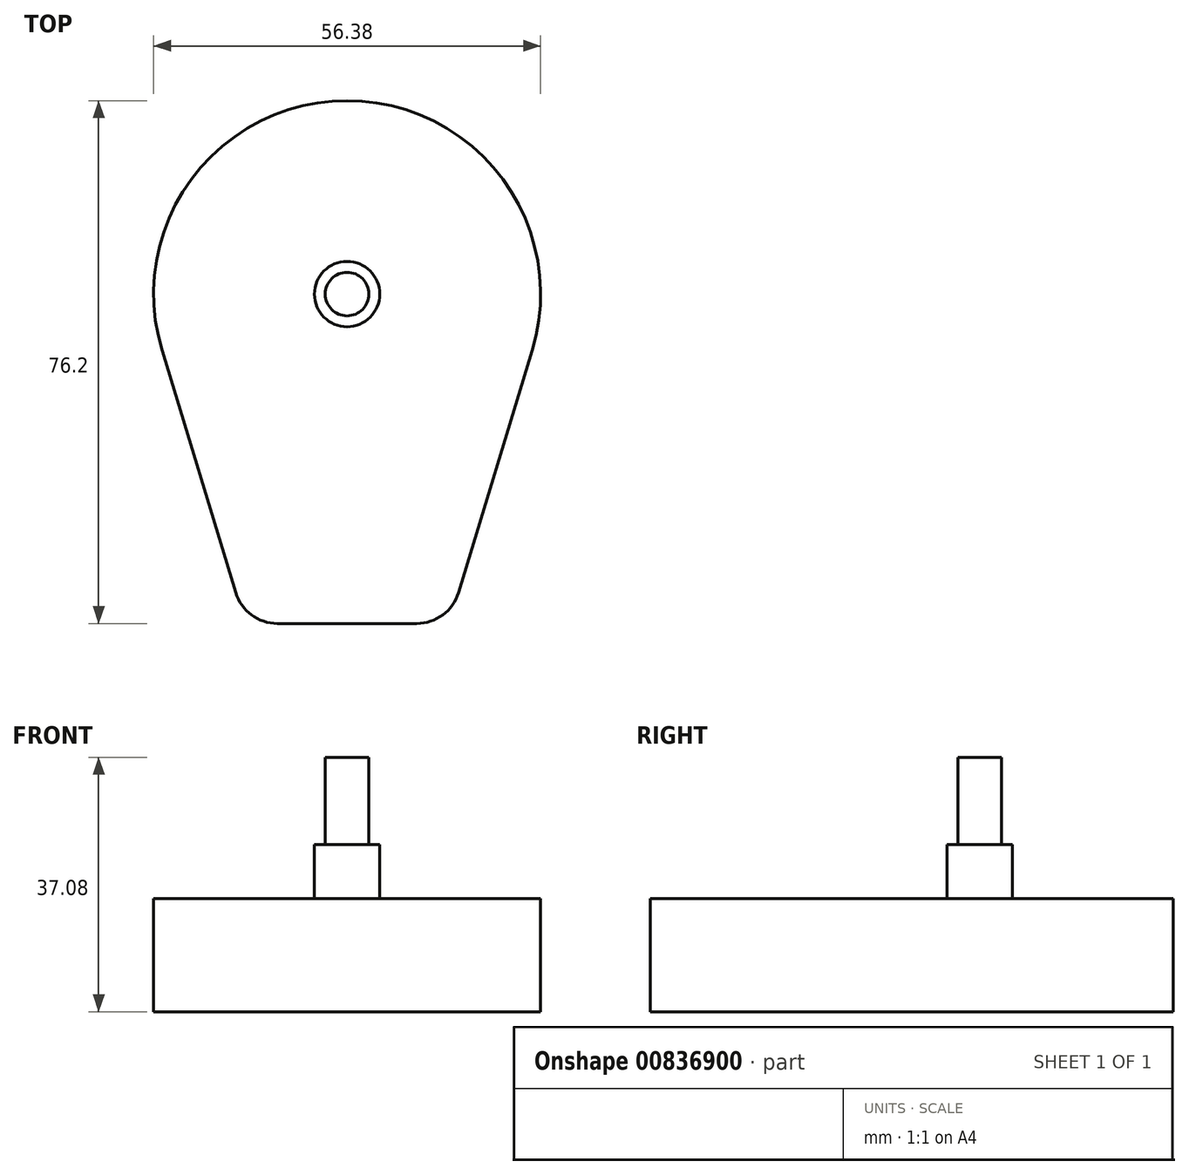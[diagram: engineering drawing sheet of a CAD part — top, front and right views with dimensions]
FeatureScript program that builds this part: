
annotation { "Feature Type Name" : "Feature", "Feature Type Description" : "" }
export const myFeature = defineFeature(function(context is Context, id is Id, definition is map)
    precondition{}
    {
        {
            var Q0;
            Q0=qCreatedBy(makeId("Top.planeOp"),FACE);
            var sketch = newSketch(context, id + "F0", { "sketchPlane" : qUnion([Q0])});
            skArc(sketch, "E0", {"start": v(26.97, -8.2) * mm, "mid": v(0, 28.2) * mm, "end": v(-26.97, -8.2) * mm});
            skLineSegment(sketch, "E1.bottom", {"start": v(14.86, -48) * mm, "end": v(-14.86, -48) * mm});
            skPoint(sketch, "E1.middle", {"position": v(0, -22.9) * mm});
            skLineSegment(sketch, "E2", {"start": v(0, -22.9) * mm, "end": v(0, 0) * mm, "construction": true});
            skPoint(sketch, "E1.top.end.orphan", {"position": v(-14.86, 2.22) * mm});
            skPoint(sketch, "E3.orphan", {"position": v(14.86, 2.22) * mm});
            skLineSegment(sketch, "E4", {"start": v(-14.86, -48) * mm, "end": v(-26.97, -8.2) * mm});
            skLineSegment(sketch, "E5", {"start": v(26.97, -8.2) * mm, "end": v(14.86, -48) * mm});
            skSolve(sketch);
        }
        {
            var Q0;
            Q0 = qSketchRegion(id + "F0", true);
            extrude(context, id + "F1", {"entities" : qUnion([Q0]), "depth" : 16.5 * mm, "offsetDistance" : 25.4 * mm});
        }
        {
            var Q0;
            Q0=makeQuery(id+"F1.opExtrude","CAP_FACE",FACE,{"disambiguationData":[OSD([sQuery(id+"F0.wireOp",EDGE,"E0"),sQuery(id+"F0.wireOp",EDGE,"E1.bottom"),sQuery(id+"F0.wireOp",EDGE,"E1.left"),sQuery(id+"F0.wireOp",EDGE,"E1.right")])],"isStart":false});
            var sketch = newSketch(context, id + "F2", { "sketchPlane" : qUnion([Q0])});
            skCircle(sketch, "E6", {"center": v(0, 0) * mm, "radius": 3.18 * mm});
            skSolve(sketch);
        }
        {
            var Q0;
            Q0 = qSketchRegion(id + "F2", true);
            extrude(context, id + "F3", {"entities" : qUnion([Q0]), "operationType" : NewBodyOperationType.ADD, "depth" : 20.57 * mm, "offsetDistance" : 25.4 * mm});
        }
        {
            var Q0;
            Q0=makeQuery(id+"F1.opExtrude","CAP_FACE",FACE,{"disambiguationData":[OSD([sQuery(id+"F0.wireOp",EDGE,"E0"),sQuery(id+"F0.wireOp",EDGE,"E1.bottom"),sQuery(id+"F0.wireOp",EDGE,"E1.left"),sQuery(id+"F0.wireOp",EDGE,"E1.right")])],"isStart":false});
            var sketch = newSketch(context, id + "F4", { "sketchPlane" : qUnion([Q0])});
            skCircle(sketch, "E7", {"center": v(0, 0) * mm, "radius": 4.76 * mm});
            skSolve(sketch);
        }
        {
            var Q0;
            Q0 = qSketchRegion(id + "F4", true);
            extrude(context, id + "F5", {"entities" : qUnion([Q0]), "operationType" : NewBodyOperationType.ADD, "depth" : 7.87 * mm, "offsetDistance" : 25.4 * mm});
        }
        {
            var Q0;
            Q0=makeQuery(id+"F1.opExtrude","SWEPT_EDGE",EDGE,{"disambiguationData":[OSD([sQuery(id+"F0.wireOp",EDGE,"E1.bottom"),sQuery(id+"F0.wireOp",EDGE,"E4")])]});
            var Q1;
            Q1=makeQuery(id+"F1.opExtrude","SWEPT_EDGE",EDGE,{"disambiguationData":[OSD([sQuery(id+"F0.wireOp",EDGE,"E1.bottom"),sQuery(id+"F0.wireOp",EDGE,"E5")])]});
            fillet(context, id + "F6", {"entities" : qUnion([Q0, Q1]), "radius" : 6.35 * mm, "tangentPropagation" : true, "allowEdgeOverflow" : false});
        }
    });
